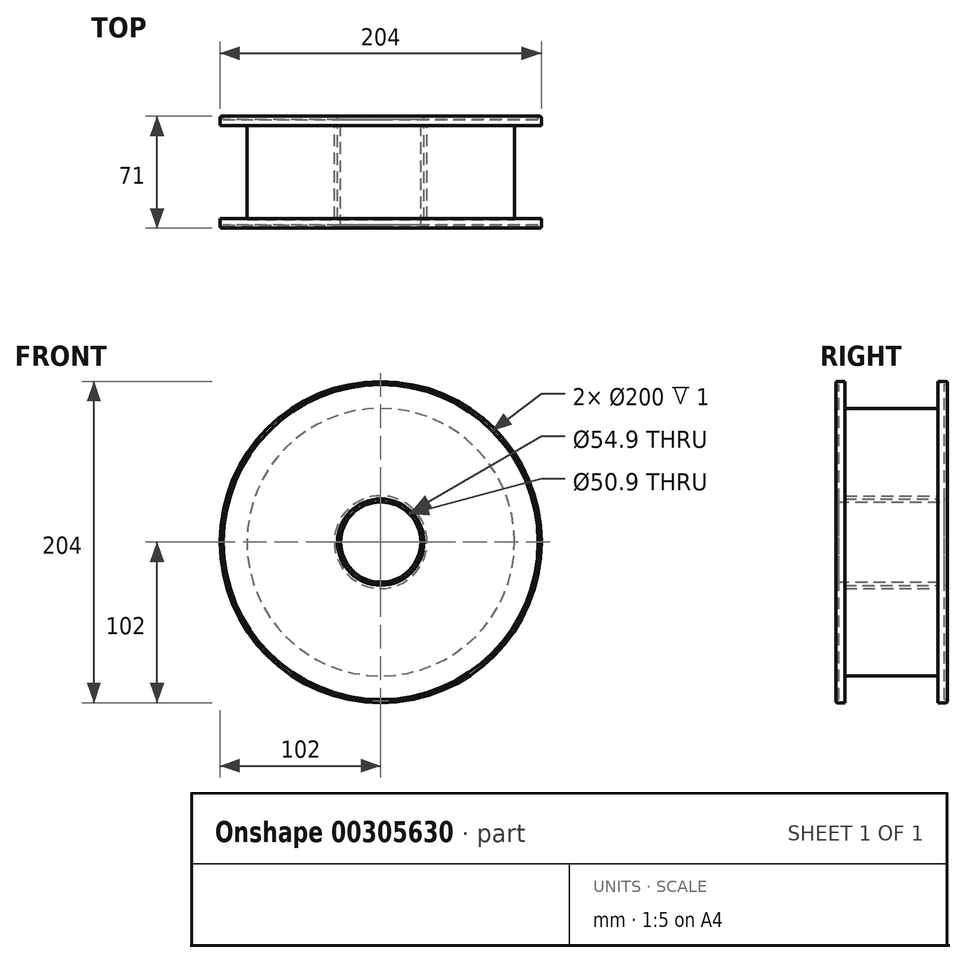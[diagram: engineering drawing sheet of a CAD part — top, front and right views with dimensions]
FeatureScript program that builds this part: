
annotation { "Feature Type Name" : "Feature", "Feature Type Description" : "" }
export const myFeature = defineFeature(function(context is Context, id is Id, definition is map)
    precondition{}
    {
        {
            var Q0;
            Q0=qCreatedBy(makeId("Front.planeOp"),FACE);
            var sketch = newSketch(context, id + "F0", { "sketchPlane" : qUnion([Q0])});
            skCircle(sketch, "E0", {"center": v(0, 0) * mm, "radius": 102 * mm});
            skCircle(sketch, "E1", {"center": v(0, 0) * mm, "radius": 25.45 * mm});
            skCircle(sketch, "E2.0", {"center": v(0, 0) * mm, "radius": 27.45 * mm});
            skCircle(sketch, "E3.0", {"center": v(0, 0) * mm, "radius": 100 * mm});
            skCircle(sketch, "E4.0", {"center": v(0, 0) * mm, "radius": 85 * mm});
            skSolve(sketch);
        }
        {
            var Q0;
            Q0=makeQuery(id+"F0.imprint","IMPRINT",FACE,{"disambiguationData":[TD([[makeQuery(id+"F0.imprint","IMPRINT",EDGE,{"derivedFrom":sQuery(id+"F0.wireOp",EDGE,"E2.0")}),-1.0]])]});
            var Q1;
            Q1=makeQuery(id+"F0.imprint","IMPRINT",FACE,{"disambiguationData":[TD([[makeQuery(id+"F0.imprint","IMPRINT",EDGE,{"derivedFrom":sQuery(id+"F0.wireOp",EDGE,"E3.0")}),1.0]])]});
            extrude(context, id + "F1", {"entities" : qUnion([Q0, Q1]), "endBound" : BoundingType.SYMMETRIC, "depth" : 67 * mm});
        }
        {
            var Q0;
            Q0=makeQuery(id+"F0.imprint","IMPRINT",FACE,{"disambiguationData":[TD([[makeQuery(id+"F0.imprint","IMPRINT",EDGE,{"derivedFrom":sQuery(id+"F0.wireOp",EDGE,"E0")}),1.0]])]});
            var Q1;
            Q1=makeQuery(id+"F0.imprint","IMPRINT",FACE,{"disambiguationData":[TD([[makeQuery(id+"F0.imprint","IMPRINT",EDGE,{"derivedFrom":sQuery(id+"F0.wireOp",EDGE,"E1")}),-1.0]])]});
            extrude(context, id + "F2", {"entities" : qUnion([Q0, Q1]), "operationType" : NewBodyOperationType.ADD, "endBound" : BoundingType.SYMMETRIC, "depth" : 71 * mm});
        }
        {
            var Q0;
            Q0=makeQuery(id+"F2.opExtrude","SWEPT_FACE",FACE,{"disambiguationData":[OSD([sQuery(id+"F0.wireOp",EDGE,"E0")])]});
            shell(context, id + "F3", {"entities" : qUnion([Q0]), "thickness" : 4 * mm});
        }
        {
            var Q0;
            Q0=makeQuery(id+"F0.imprint","IMPRINT",FACE,{"disambiguationData":[TD([[makeQuery(id+"F0.imprint","IMPRINT",EDGE,{"derivedFrom":sQuery(id+"F0.wireOp",EDGE,"E2.0")}),-1.0]])]});
            extrude(context, id + "F4", {"entities" : qUnion([Q0]), "endBound" : BoundingType.SYMMETRIC, "depth" : 60 * mm});
        }
        {
            var Q0;
            Q0=makeQuery(id+"F2.opExtrude","CAP_FACE",FACE,{"disambiguationData":[OSD([sQuery(id+"F0.wireOp",EDGE,"E0"),sQuery(id+"F0.wireOp",EDGE,"E3.0")])],"isStart":false});
            var Q1;
            Q1=makeQuery(id+"F2.opExtrude","CAP_FACE",FACE,{"disambiguationData":[OSD([sQuery(id+"F0.wireOp",EDGE,"E1"),sQuery(id+"F0.wireOp",EDGE,"E2.0")])],"isStart":false});
            var Q2;
            Q2=makeQuery(id+"F2.opExtrude","CAP_FACE",FACE,{"disambiguationData":[OSD([sQuery(id+"F0.wireOp",EDGE,"E1"),sQuery(id+"F0.wireOp",EDGE,"E2.0")])],"isStart":true});
            var Q3;
            Q3=makeQuery(id+"F2.opExtrude","CAP_FACE",FACE,{"disambiguationData":[OSD([sQuery(id+"F0.wireOp",EDGE,"E0"),sQuery(id+"F0.wireOp",EDGE,"E3.0")])],"isStart":true});
            fillet(context, id + "F5", {"entities" : qUnion([Q0, Q1, Q2, Q3]), "radius" : 1 * mm, "tangentPropagation" : true, "allowEdgeOverflow" : false});
        }
    });
